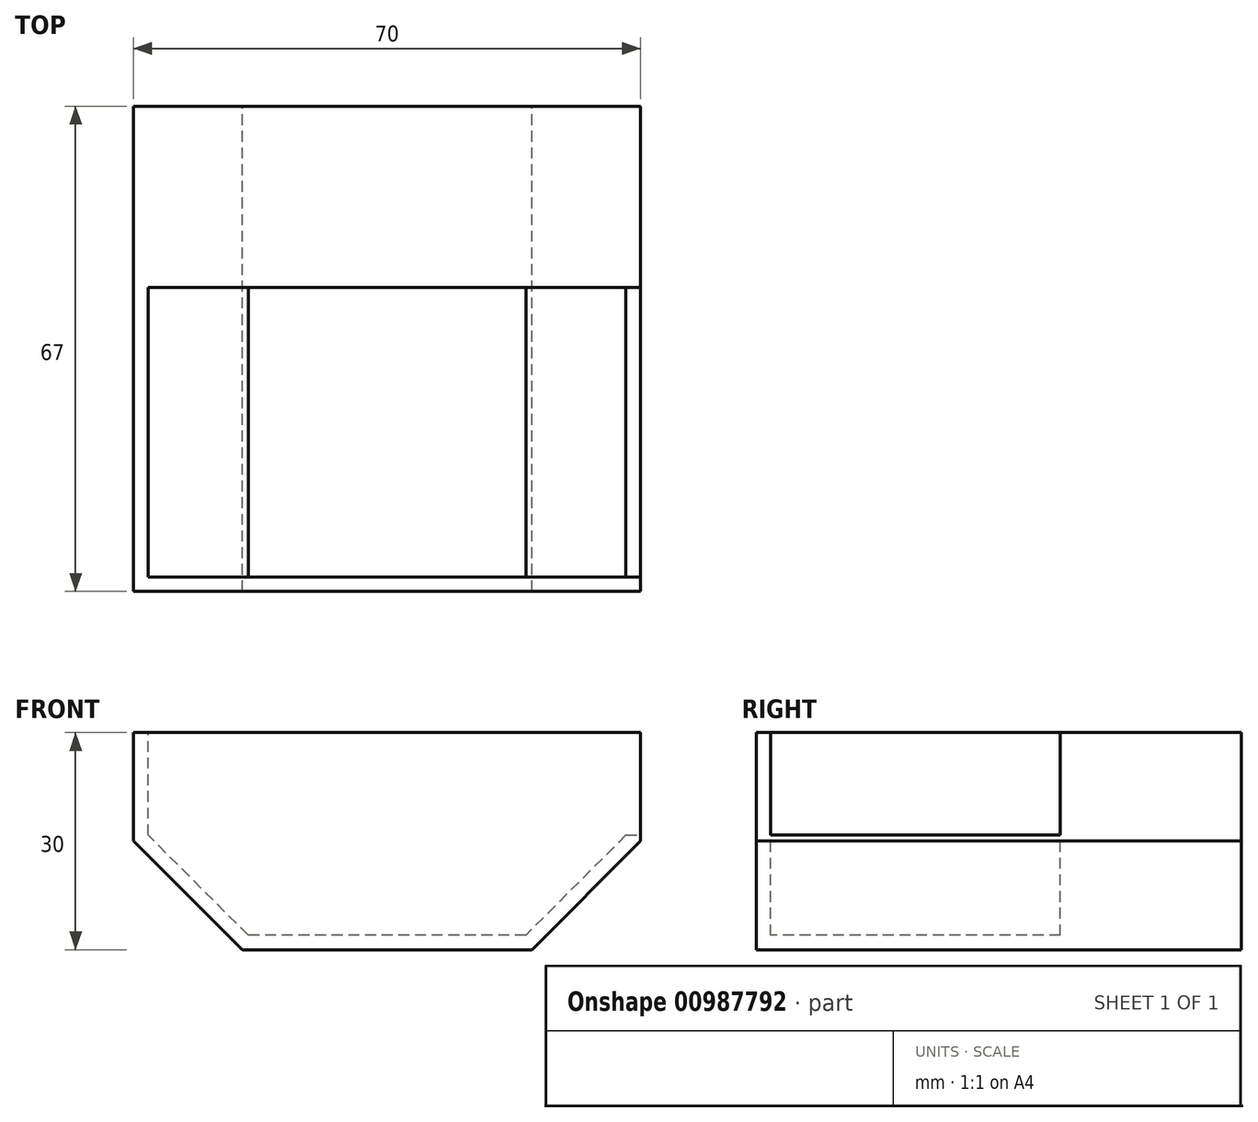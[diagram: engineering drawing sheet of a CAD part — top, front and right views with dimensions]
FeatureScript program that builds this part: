
annotation { "Feature Type Name" : "Feature", "Feature Type Description" : "" }
export const myFeature = defineFeature(function(context is Context, id is Id, definition is map)
    precondition{}
    {
        {
            var Q0;
            Q0=qCreatedBy(makeId("Front.planeOp"),FACE);
            var sketch = newSketch(context, id + "F0", { "sketchPlane" : qUnion([Q0])});
            skLineSegment(sketch, "E0", {"start": v(35, 0) * mm, "end": v(-35, 0) * mm});
            skLineSegment(sketch, "E1", {"start": v(35, 0) * mm, "end": v(35, -15) * mm});
            skLineSegment(sketch, "E2", {"start": v(35, -15) * mm, "end": v(20, -30) * mm});
            skLineSegment(sketch, "E3", {"start": v(20, -30) * mm, "end": v(-20, -30) * mm});
            skLineSegment(sketch, "E4", {"start": v(-35, 0) * mm, "end": v(-35, -15) * mm});
            skLineSegment(sketch, "E5", {"start": v(-35, -15) * mm, "end": v(-20, -30) * mm});
            skSolve(sketch);
        }
        {
            var Q0;
            Q0=makeQuery(id+"F0.imprint","IMPRINT",FACE,{"disambiguationData":[TD([[makeQuery(id+"F0.imprint","IMPRINT",EDGE,{"derivedFrom":sQuery(id+"F0.wireOp",EDGE,"E0")}),1.0]])]});
            extrude(context, id + "F1", {"entities" : qUnion([Q0]), "depth" : 2 * mm, "offsetDistance" : 25 * mm});
        }
        {
            var Q0;
            Q0=makeQuery(id+"F1.opExtrude","CAP_FACE",FACE,{"disambiguationData":[OSD([sQuery(id+"F0.wireOp",EDGE,"E0"),sQuery(id+"F0.wireOp",EDGE,"E1"),sQuery(id+"F0.wireOp",EDGE,"E2"),sQuery(id+"F0.wireOp",EDGE,"E3"),sQuery(id+"F0.wireOp",EDGE,"E4"),sQuery(id+"F0.wireOp",EDGE,"E5")])],"isStart":true});
            var sketch = newSketch(context, id + "F2", { "sketchPlane" : qUnion([Q0])});
            skLineSegment(sketch, "E6.0", {"start": v(19.17, -28) * mm, "end": v(33, -14.17) * mm});
            skLineSegment(sketch, "E6.2", {"start": v(-33, -2) * mm, "end": v(-33, -14.17) * mm});
            skLineSegment(sketch, "E6.3", {"start": v(33, -14.17) * mm, "end": v(33, -2) * mm});
            skLineSegment(sketch, "E6.4", {"start": v(-33, -14.17) * mm, "end": v(-19.17, -28) * mm});
            skLineSegment(sketch, "E6.5", {"start": v(-19.17, -28) * mm, "end": v(19.17, -28) * mm});
            skLineSegment(sketch, "E7", {"start": v(-33, -2) * mm, "end": v(-33, 0) * mm});
            skLineSegment(sketch, "E8", {"start": v(33, -2) * mm, "end": v(33, 0) * mm});
            skLineSegment(sketch, "E9", {"start": v(-33, -14.17) * mm, "end": v(-35, -14.17) * mm});
            skSolve(sketch);
        }
        {
            var Q0;
            Q0=makeQuery(id+"F2.imprint","IMPRINT",FACE,{"disambiguationData":[TD([[makeQuery(id+"F2.imprint","IMPRINT",EDGE,{"derivedFrom":sQuery(id+"F2.wireOp",EDGE,"E6.0")}),-1.0]])]});
            extrude(context, id + "F3", {"entities" : qUnion([Q0]), "operationType" : NewBodyOperationType.ADD, "depth" : 40 * mm, "offsetDistance" : 25 * mm});
        }
        {
            var Q0;
            Q0=makeQuery(id+"F3.opExtrude","CAP_FACE",FACE,{"disambiguationData":[OSD([sQuery(id+"F0.wireOp",EDGE,"E0"),sQuery(id+"F0.wireOp",EDGE,"E1"),sQuery(id+"F0.wireOp",EDGE,"E2"),sQuery(id+"F0.wireOp",EDGE,"E3"),sQuery(id+"F0.wireOp",EDGE,"E4"),sQuery(id+"F0.wireOp",EDGE,"E5"),sQuery(id+"F2.wireOp",EDGE,"E6.0"),sQuery(id+"F2.wireOp",EDGE,"E6.3"),sQuery(id+"F2.wireOp",EDGE,"E6.4"),sQuery(id+"F2.wireOp",EDGE,"E6.5"),sQuery(id+"F2.wireOp",EDGE,"E8"),sQuery(id+"F2.wireOp",EDGE,"E9")])],"isStart":false});
            var sketch = newSketch(context, id + "F4", { "sketchPlane" : qUnion([Q0])});
            skLineSegment(sketch, "E10.0.0", {"start": v(19.17, -28) * mm, "end": v(33, -14.17) * mm});
            skLineSegment(sketch, "E10.0.1", {"start": v(33, -14.17) * mm, "end": v(33, 0) * mm});
            skLineSegment(sketch, "E10.0.2", {"start": v(33, 0) * mm, "end": v(-35, 0) * mm});
            skLineSegment(sketch, "E10.0.3", {"start": v(-35, 0) * mm, "end": v(-35, -14.17) * mm});
            skLineSegment(sketch, "E10.0.4", {"start": v(-35, -14.17) * mm, "end": v(-33, -14.17) * mm});
            skLineSegment(sketch, "E10.0.5", {"start": v(-33, -14.17) * mm, "end": v(-19.17, -28) * mm});
            skLineSegment(sketch, "E10.0.6", {"start": v(-19.17, -28) * mm, "end": v(19.17, -28) * mm});
            skSolve(sketch);
        }
        {
            var Q0;
            Q0 = qSketchRegion(id + "F4", true);
            var Q1;
            Q1=makeQuery(id+"F4.imprint","IMPRINT",FACE,{"disambiguationData":[TD([[makeQuery(id+"F4.imprint","IMPRINT",EDGE,{"derivedFrom":sQuery(id+"F4.wireOp",EDGE,"E10.0.0")}),-1.0]])]});
            extrude(context, id + "F5", {"entities" : qUnion([Q0, Q1]), "operationType" : NewBodyOperationType.ADD, "depth" : 25 * mm, "offsetDistance" : 25 * mm});
        }
    });
